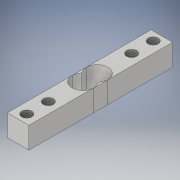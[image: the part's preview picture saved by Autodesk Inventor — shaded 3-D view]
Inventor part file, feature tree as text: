
AUTODESK INVENTOR PART (.ipt)
format: ipt  version: 2019 (Build 230136000, 136)  size: 142,336 bytes
history: native  units: mm
features: thread x4, extrude x2, sketch x2
ambient origin geometry x8: Origin, YZ Plane, XZ Plane, XY Plane, X Axis, Y Axis, Z Axis, Center Point
bodies: Solid1 (feature_tree)
feature tree (8):
  extrude  "Extrusion1"  Depth=15.0mm
  extrude  "Extrusion2"  Depth=15.0mm
  thread  "Thread1"  [1 undecoded]
  thread  "Thread2"  [1 undecoded]
  thread  "Thread3"  [1 undecoded]
  thread  "Thread4"  [1 undecoded]
  sketch  "Sketch2"  dims[d0=15.0mm d1=15.0mm]
  sketch  "Sketch3"  dims[d2=10.0mm d3=15.0mm d4=7.5mm d5=100.0mm d6=50.0mm d7=55.0mm d8=15.0mm d9=0.0mm d10=7.0mm d11=7.0mm d12=15.0mm d13=7.5mm d14=6.0mm d15=21.0mm d16=7.0mm d17=7.0mm d18=15.0mm d19=6.0mm d20=7.5mm d21=21.0mm d22=15.0mm d23=0.0mm d24=10.0mm d25=0.0mm d26=10.0mm d27=0.0mm d28=10.0mm d29=0.0mm d30=10.0mm d31=0.0mm]
note: 4 required parameter values undecoded (feature->parameter linkage not recoverable at this tier; creation-order binding heuristic only, values carry confidence <= 0.55)
